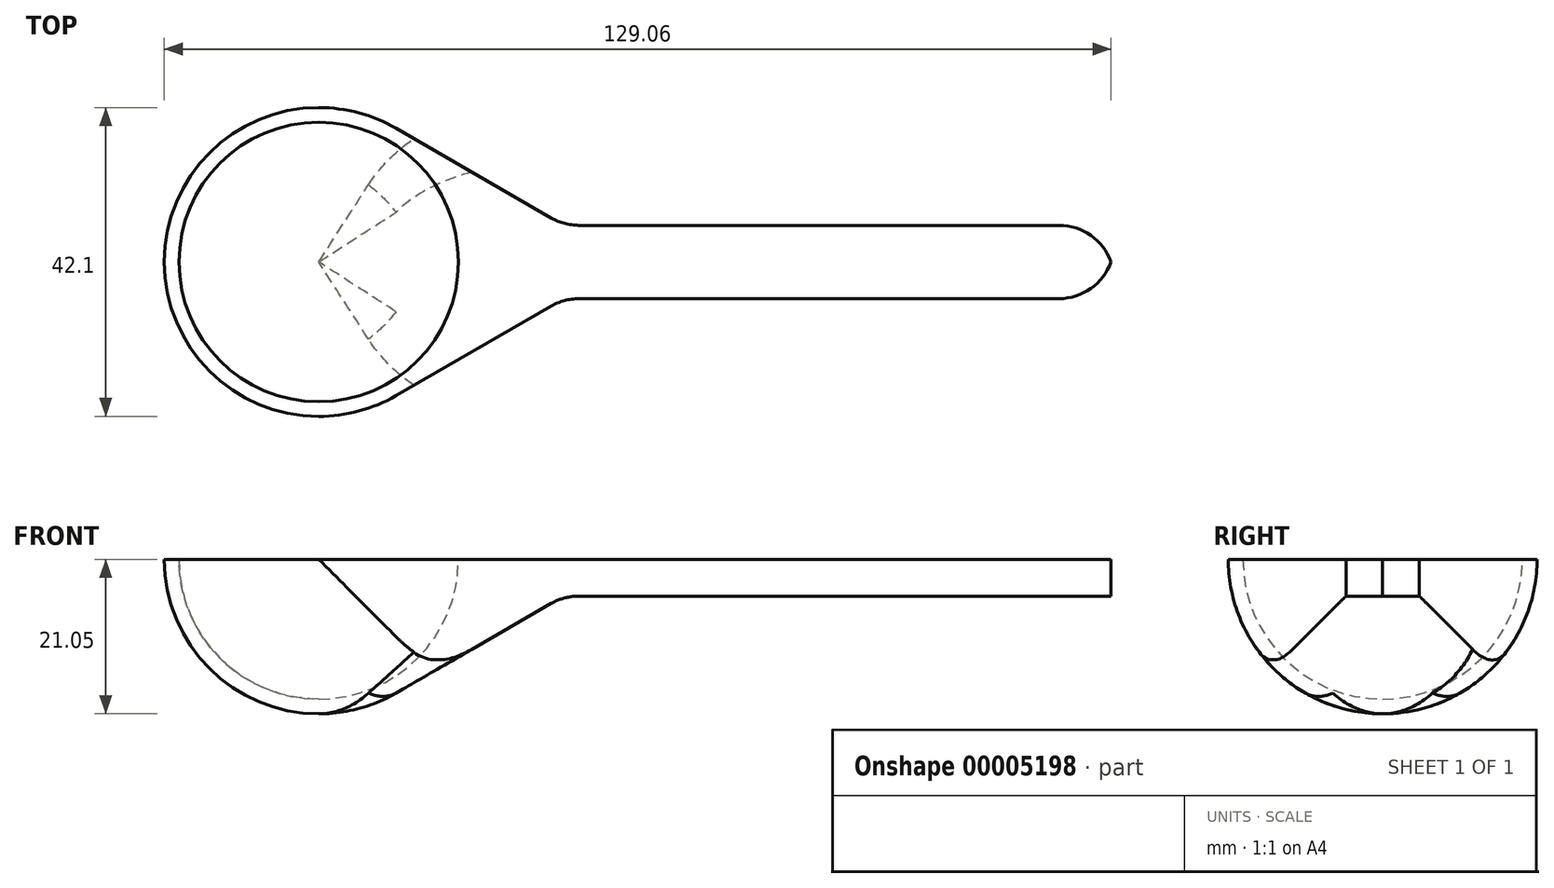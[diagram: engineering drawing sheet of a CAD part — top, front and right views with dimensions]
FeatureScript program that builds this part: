
annotation { "Feature Type Name" : "Feature", "Feature Type Description" : "" }
export const myFeature = defineFeature(function(context is Context, id is Id, definition is map)
    precondition{}
    {
        {
            var Q0;
            Q0=qCreatedBy(makeId("Front.planeOp"),FACE);
            var sketch = newSketch(context, id + "F0", { "sketchPlane" : qUnion([Q0])});
            skCircle(sketch, "E0", {"center": v(0, 0) * mm, "radius": 19.05 * mm, "construction": true});
            skCircle(sketch, "E1", {"center": v(0, 0) * mm, "radius": 21.05 * mm, "construction": true});
            skLineSegment(sketch, "E2", {"start": v(0, 0) * mm, "end": v(0, 19.05) * mm, "construction": true});
            skArc(sketch, "E3", {"start": v(-19.05, 0) * mm, "mid": v(-13.47, -13.47) * mm, "end": v(0, -19.05) * mm});
            skArc(sketch, "E4", {"start": v(-21.05, 0) * mm, "mid": v(-14.88, -14.88) * mm, "end": v(0, -21.05) * mm});
            skLineSegment(sketch, "E5", {"start": v(-21.05, 0) * mm, "end": v(-19.05, 0) * mm});
            skLineSegment(sketch, "E6", {"start": v(0, -19.05) * mm, "end": v(0, -21.05) * mm});
            skSolve(sketch);
        }
        {
            var Q0;
            Q0 = qSketchRegion(id + "F0", true);
            var Q1;
            Q1=sQuery(id+"F0.wireOp",EDGE,"E6");
            revolve(context, id + "F1", {"entities" : qUnion([Q0]), "axis" : qUnion([Q1]), "revolveType" : RevolveType.FULL});
        }
        {
            var Q0;
            Q0=qCreatedBy(makeId("Front.planeOp"),FACE);
            var sketch = newSketch(context, id + "F2", { "sketchPlane" : qUnion([Q0])});
            skCircle(sketch, "E7", {"center": v(0, 0) * mm, "radius": 19.05 * mm, "construction": true});
            skCircle(sketch, "E8", {"center": v(0, 0) * mm, "radius": 21.05 * mm, "construction": true});
            skLineSegment(sketch, "E9", {"start": v(0, 0) * mm, "end": v(0, -21.05) * mm});
            skArc(sketch, "E10", {"start": v(0, -21.05) * mm, "mid": v(5.45, -20.33) * mm, "end": v(10.53, -18.23) * mm});
            skLineSegment(sketch, "E11", {"start": v(10.53, -18.23) * mm, "end": v(33.44, -5) * mm});
            skLineSegment(sketch, "E12", {"start": v(33.44, -5) * mm, "end": v(33.44, 0) * mm});
            skLineSegment(sketch, "E13", {"start": v(33.44, 0) * mm, "end": v(0, 0) * mm});
            skSolve(sketch);
        }
        {
            var Q0;
            Q0 = qSketchRegion(id + "F2", true);
            extrude(context, id + "F3", {"entities" : qUnion([Q0]), "operationType" : NewBodyOperationType.ADD, "depth" : (25.4 * 1.5 + 4) * mm, "symmetric" : true});
        }
        {
            var Q0;
            Q0=makeQuery(id+"F3.boolean.opBoolean","SPLIT",FACE,{"disambiguationData":[TD([makeQuery(id+"F1.opRevolve","SWEPT_FACE",FACE,{"disambiguationData":[OSD([sQuery(id+"F0.wireOp",EDGE,"E3")])]})])],"derivedFrom":makeQuery(id+"F3.opExtrude","SWEPT_FACE",FACE,{"disambiguationData":[OSD([sQuery(id+"F2.wireOp",EDGE,"E9")])]})});
            var sketch = newSketch(context, id + "F4", { "sketchPlane" : qUnion([Q0])});
            skArc(sketch, "E14", {"start": v(19.05, 0) * mm, "mid": v(13.47, -13.47) * mm, "end": v(0, -19.05) * mm});
            skLineSegment(sketch, "E15", {"start": v(0, -19.05) * mm, "end": v(0, 0) * mm});
            skLineSegment(sketch, "E16", {"start": v(19.05, 0) * mm, "end": v(0, 0) * mm});
            skSolve(sketch);
        }
        {
            var Q0;
            Q0 = qSketchRegion(id + "F4", true);
            var Q1;
            Q1=sQuery(id+"F4.wireOp",EDGE,"E15");
            revolve(context, id + "F5", {"operationType" : NewBodyOperationType.REMOVE, "entities" : qUnion([Q0]), "axis" : qUnion([Q1]), "revolveType" : RevolveType.FULL, "oppositeDirection" : true});
        }
        {
            var Q0;
            {var subQ0=sQuery(id+"F2.wireOp",EDGE,"E13");var subQ1=sQuery(id+"F2.wireOp",EDGE,"E10");var subQ2=sQuery(id+"F2.wireOp",EDGE,"E9");var subQ3=makeQuery(id+"F3.opExtrude","SWEPT_FACE",FACE,{"disambiguationData":[OSD([subQ2])]});Q0=makeQuery(id+"F3.boolean.opBoolean","SPLIT",FACE,{"disambiguationData":[TD([makeQuery(id+"F3.opExtrude","CAP_FACE",FACE,{"disambiguationData":[OSD([subQ2,subQ1,sQuery(id+"F2.wireOp",EDGE,"E11"),sQuery(id+"F2.wireOp",EDGE,"E12"),subQ0])],"isStart":false})])],"derivedFrom":subQ3});}
            var sketch = newSketch(context, id + "F6", { "sketchPlane" : qUnion([Q0])});
            skArc(sketch, "E17", {"start": v(21.05, 0) * mm, "mid": v(14.88, -14.88) * mm, "end": v(0, -21.05) * mm});
            skLineSegment(sketch, "E18.0", {"start": v(21.05, -21.05) * mm, "end": v(0, -21.05) * mm});
            skLineSegment(sketch, "E18.1", {"start": v(21.05, 0) * mm, "end": v(21.05, -21.05) * mm});
            skLineSegment(sketch, "E19", {"start": v(0, -21.05) * mm, "end": v(0, 0) * mm, "construction": true});
            skArc(sketch, "E20.MirrorCS", {"start": v(-21.05, 0) * mm, "mid": v(-14.88, -14.88) * mm, "end": v(0, -21.05) * mm});
            skLineSegment(sketch, "E21.MirrorCS", {"start": v(-21.05, -21.05) * mm, "end": v(0, -21.05) * mm});
            skLineSegment(sketch, "E22.MirrorCS", {"start": v(-21.05, 0) * mm, "end": v(-21.05, -21.05) * mm});
            skSolve(sketch);
        }
        {
            var Q0;
            Q0 = qSketchRegion(id + "F6", true);
            extrude(context, id + "F7", {"entities" : qUnion([Q0]), "operationType" : NewBodyOperationType.REMOVE, "endBound" : BoundingType.THROUGH_ALL, "oppositeDirection" : true, "depth" : 25 * mm});
        }
        {
            var Q0;
            Q0=makeQuery(id+"F3.boolean.opBoolean","MERGE",FACE,{"derivedFrom":[makeQuery(id+"F1.opRevolve","SWEPT_FACE",FACE,{"disambiguationData":[OSD([sQuery(id+"F0.wireOp",EDGE,"E5")])]}),makeQuery(id+"F3.opExtrude","SWEPT_FACE",FACE,{"disambiguationData":[OSD([sQuery(id+"F2.wireOp",EDGE,"E13")])]})]});
            var sketch = newSketch(context, id + "F8", { "sketchPlane" : qUnion([Q0])});
            skLineSegment(sketch, "E23", {"start": v(0, 0) * mm, "end": v(19.05, 0) * mm, "construction": true});
            skArc(sketch, "E24", {"start": v(0, -21.05) * mm, "mid": v(5.45, -20.33) * mm, "end": v(10.53, -18.23) * mm});
            skLineSegment(sketch, "E25", {"start": v(0, -21.05) * mm, "end": v(33.44, -21.05) * mm});
            skLineSegment(sketch, "E26", {"start": v(10.53, -18.23) * mm, "end": v(33.44, -5) * mm});
            skLineSegment(sketch, "E27", {"start": v(33.44, -21.05) * mm, "end": v(33.44, -5) * mm});
            skArc(sketch, "E28.MirrorCS", {"start": v(0, 21.05) * mm, "mid": v(5.45, 20.33) * mm, "end": v(10.53, 18.23) * mm});
            skLineSegment(sketch, "E29.MirrorCS", {"start": v(33.44, 21.05) * mm, "end": v(33.44, 5) * mm});
            skLineSegment(sketch, "E30.MirrorCS", {"start": v(10.53, 18.23) * mm, "end": v(33.44, 5) * mm});
            skLineSegment(sketch, "E31.MirrorCS", {"start": v(0, 21.05) * mm, "end": v(33.44, 21.05) * mm});
            skSolve(sketch);
        }
        {
            var Q0;
            Q0 = qSketchRegion(id + "F8", true);
            extrude(context, id + "F9", {"entities" : qUnion([Q0]), "operationType" : NewBodyOperationType.REMOVE, "endBound" : BoundingType.THROUGH_ALL, "oppositeDirection" : true, "depth" : 25 * mm});
        }
        {
            var Q0;
            Q0=makeQuery(id+"F3.opExtrude","SWEPT_FACE",FACE,{"disambiguationData":[OSD([sQuery(id+"F2.wireOp",EDGE,"E12")])]});
            var sketch = newSketch(context, id + "F10", { "sketchPlane" : qUnion([Q0])});
            skLineSegment(sketch, "E32.0", {"start": v(-5, 0) * mm, "end": v(5, 0) * mm});
            skLineSegment(sketch, "E32.1", {"start": v(5, -5) * mm, "end": v(5, 0) * mm});
            skLineSegment(sketch, "E32.2", {"start": v(-5, -5) * mm, "end": v(5, -5) * mm});
            skLineSegment(sketch, "E32.3", {"start": v(-5, -5) * mm, "end": v(-5, 0) * mm});
            skSolve(sketch);
        }
        {
            var Q0;
            Q0 = qSketchRegion(id + "F10", true);
            extrude(context, id + "F11", {"entities" : qUnion([Q0]), "operationType" : NewBodyOperationType.ADD, "depth" : 75 * mm});
        }
        {
            var Q0;
            Q0=makeQuery(id+"F11.opExtrude","CAP_EDGE",EDGE,{"disambiguationData":[OSD([sQuery(id+"F10.wireOp",EDGE,"E32.3")])],"isStart":false});
            var Q1;
            Q1=makeQuery(id+"F11.opExtrude","CAP_EDGE",EDGE,{"disambiguationData":[OSD([sQuery(id+"F10.wireOp",EDGE,"E32.1")])],"isStart":false});
            var Q2;
            Q2=makeQuery(id+"F11.boolean.opBoolean","MERGE",EDGE,{"derivedFrom":[makeQuery(id+"F9.boolean.opBoolean","COPY",EDGE,{"derivedFrom":makeQuery(id+"F9.opExtrude","SWEPT_EDGE",EDGE,{"disambiguationData":[OSD([sQuery(id+"F2.wireOp",EDGE,"E12"),sQuery(id+"F2.wireOp",EDGE,"E13"),sQuery(id+"F8.wireOp",EDGE,"E26"),sQuery(id+"F8.wireOp",EDGE,"E27")])]})}),makeQuery(id+"F11.opExtrude","CAP_EDGE",EDGE,{"disambiguationData":[OSD([sQuery(id+"F10.wireOp",EDGE,"E32.3")])],"isStart":true})]});
            var Q3;
            Q3=makeQuery(id+"F11.boolean.opBoolean","MERGE",EDGE,{"derivedFrom":[makeQuery(id+"F9.boolean.opBoolean","COPY",EDGE,{"derivedFrom":makeQuery(id+"F9.opExtrude","SWEPT_EDGE",EDGE,{"disambiguationData":[OSD([sQuery(id+"F2.wireOp",EDGE,"E12"),sQuery(id+"F2.wireOp",EDGE,"E13"),sQuery(id+"F8.wireOp",EDGE,"E29.MirrorCS"),sQuery(id+"F8.wireOp",EDGE,"E30.MirrorCS")])]})}),makeQuery(id+"F11.opExtrude","CAP_EDGE",EDGE,{"disambiguationData":[OSD([sQuery(id+"F10.wireOp",EDGE,"E32.1")])],"isStart":true})]});
            var Q4;
            Q4=makeQuery(id+"F11.boolean.opBoolean","MERGE",EDGE,{"derivedFrom":[makeQuery(id+"F3.opExtrude","SWEPT_EDGE",EDGE,{"disambiguationData":[OSD([sQuery(id+"F2.wireOp",EDGE,"E11"),sQuery(id+"F2.wireOp",EDGE,"E12")])]}),makeQuery(id+"F11.opExtrude","CAP_EDGE",EDGE,{"disambiguationData":[OSD([sQuery(id+"F10.wireOp",EDGE,"E32.2")])],"isStart":true})]});
            var Q5;
            Q5=makeQuery(id+"F7.boolean.opBoolean","INTERSECT",EDGE,{"derivedFrom":[makeQuery(id+"F3.opExtrude","SWEPT_FACE",FACE,{"disambiguationData":[OSD([sQuery(id+"F2.wireOp",EDGE,"E11")])]}),makeQuery(id+"F7.opExtrude","SWEPT_FACE",FACE,{"disambiguationData":[OSD([sQuery(id+"F6.wireOp",EDGE,"E17")])]})]});
            var Q6;
            Q6=makeQuery(id+"F7.boolean.opBoolean","INTERSECT",EDGE,{"derivedFrom":[makeQuery(id+"F3.opExtrude","SWEPT_FACE",FACE,{"disambiguationData":[OSD([sQuery(id+"F2.wireOp",EDGE,"E11")])]}),makeQuery(id+"F7.opExtrude","SWEPT_FACE",FACE,{"disambiguationData":[OSD([sQuery(id+"F6.wireOp",EDGE,"E20.MirrorCS")])]})]});
            fillet(context, id + "F12", {"entities" : qUnion([Q0, Q1, Q2, Q3, Q4, Q5, Q6]), "radius" : 7.5 * mm, "tangentPropagation" : true, "allowEdgeOverflow" : false});
        }
    });
